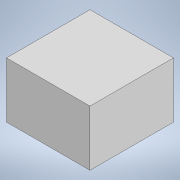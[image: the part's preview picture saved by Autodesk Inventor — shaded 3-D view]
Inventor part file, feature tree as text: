
AUTODESK INVENTOR PART (.ipt)
format: ipt  version: 2022 (Build 260153000, 153)  size: 102,400 bytes
history: native  units: in
note: dims shown in document units (in); Inventor stores cm internally (conversion verified against a paired STEP export)
features: extrude x2, sketch x2
ambient origin geometry x8: Origin, YZ Plane, XZ Plane, XY Plane, X Axis, Y Axis, Z Axis, Center Point
bodies: Solid1 (feature_tree)
feature tree (4):
  extrude  "Extrusion1"  Depth=0.1969in
  extrude  "Extrusion2"  Depth=0.2362in
  sketch  "Sketch1"  dims[d0=0.1969in d1=0.1969in]
  sketch  "Sketch2"  dims[d2=0.2362in d3=0.2362in d4=0.1181in d5=0.0in d6=0.0394in d7=0.0in]
